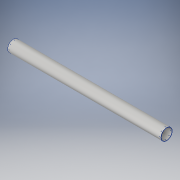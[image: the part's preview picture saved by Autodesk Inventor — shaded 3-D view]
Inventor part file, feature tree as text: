
AUTODESK INVENTOR PART (.ipt)
format: ipt  version: 2017 SP1 (Build 210196100, 196)  size: 156,160 bytes
history: native  units: in
note: dims shown in document units (in); Inventor stores cm internally (conversion verified against a paired STEP export)
features: sketch x3, hole x2, pattern_circular x2, extrude x1, plane x1
ambient origin geometry x8: Origin, YZ Plane, XZ Plane, XY Plane, X Axis, Y Axis, Z Axis, Center Point
bodies: Solid1 (feature_tree)
feature tree (9):
  extrude  "Extrusion1"  Depth=8.0in
  plane  "Work Plane1"
  hole  "Hole1"  [1 undecoded]
  pattern_circular  "Circular Pattern1"  Count=8 Angle=360.0deg
  hole  "Hole2"  [1 undecoded]
  pattern_circular  "Circular Pattern2"  Count=8 Angle=360.0deg
  sketch  "Sketch1"  dims[d0=7.5in d1=8.0in]
  sketch  "Sketch2"  dims[d2=108.0in d3=0.0in d4=1.0in]
  sketch  "Sketch3"  dims[d5=0.25in d6=0.75in d7=0.375in d8=0.25in d9=0.5635in d10=1.0in d11=0.8108in d12=3.1496in d13=360.0deg d15=1.0in d16=0.25in d17=0.75in d18=0.375in d19=0.25in d20=0.5635in d21=1.0in d22=0.8108in d23=3.1496in d24=360.0deg]
note: 2 required parameter values undecoded (feature->parameter linkage not recoverable at this tier; creation-order binding heuristic only, values carry confidence <= 0.55)
